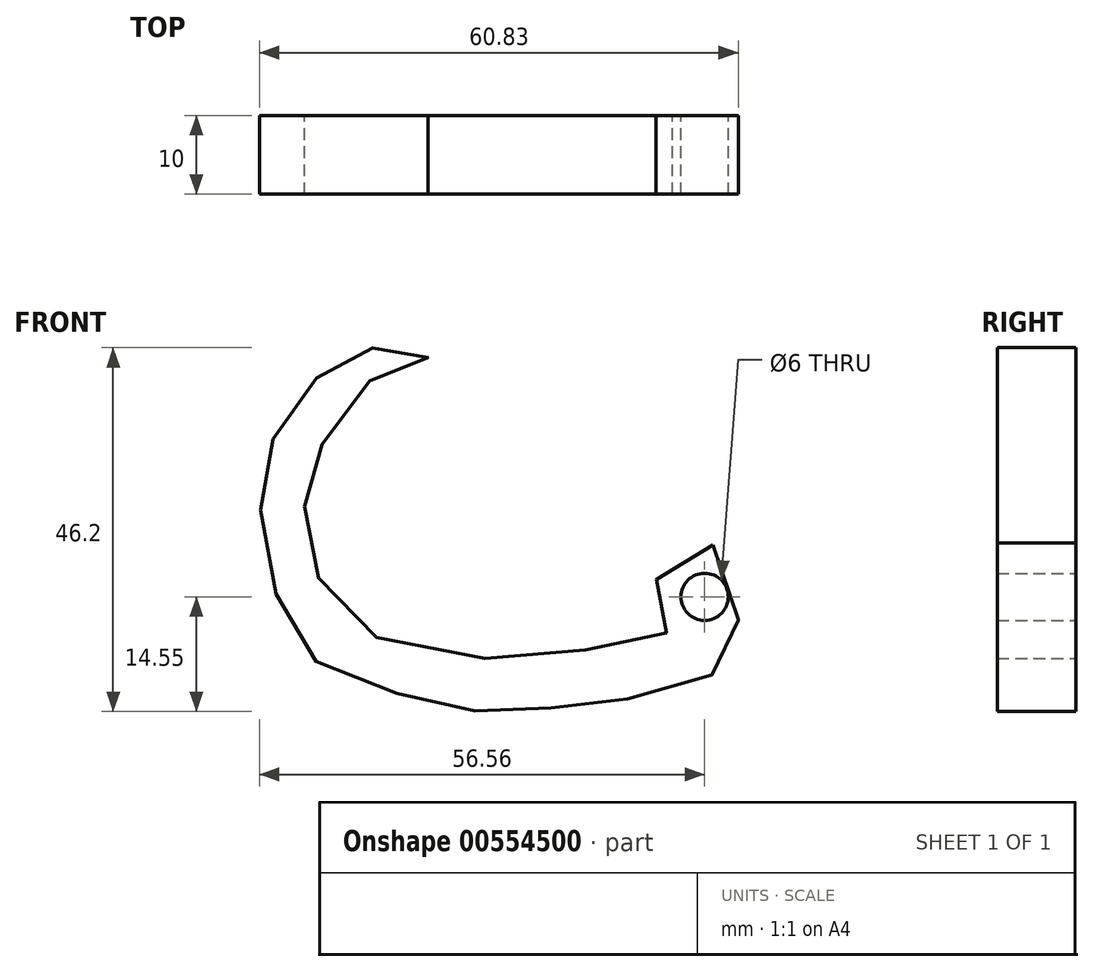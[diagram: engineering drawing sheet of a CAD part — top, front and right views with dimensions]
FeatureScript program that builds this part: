
annotation { "Feature Type Name" : "Feature", "Feature Type Description" : "" }
export const myFeature = defineFeature(function(context is Context, id is Id, definition is map)
    precondition{}
    {
        {
            var Q0;
            Q0=qCreatedBy(makeId("Front.planeOp"),FACE);
            var sketch = newSketch(context, id + "F0", { "sketchPlane" : qUnion([Q0])});
            skFitSpline(sketch, "E0", {"points": [v(32.44, 3.87) * mm, v(35.6, -6.2) * mm, v(33.3, -11.94) * mm, v(21.51, -15.68) * mm, v(11.45, -16.83) * mm, v(1.67, -17.12) * mm, v(-9.26, -14.53) * mm, v(-20.19, -9.07) * mm, v(-23.92, 1.86) * mm, v(-25.08, 12.79) * mm, v(-21.34, 20.7) * mm, v(-15.3, 27.45) * mm, v(-8.68, 28.9) * mm, v(-3.8, 27.74) * mm, v(-8.68, 26.3) * mm, v(-16.16, 18.54) * mm, v(-19.32, 11.35) * mm, v(-18.75, 3.59) * mm, v(-14.15, -5.62) * mm, v(3.97, -10.5) * mm, v(20.36, -8.78) * mm, v(27.26, -6.2) * mm, v(25.25, 0.14) * mm, v(32.44, 3.87) * mm]});
            skCircle(sketch, "E1", {"center": v(31.35, -2.7) * mm, "radius": 3 * mm});
            skSolve(sketch);
        }
        {
            var Q0;
            Q0=makeQuery(id+"F0.imprint","IMPRINT",FACE,{"disambiguationData":[TD([[makeQuery(id+"F0.imprint","IMPRINT",EDGE,{"derivedFrom":sQuery(id+"F0.wireOp",EDGE,"E0")}),-1.0]])]});
            extrude(context, id + "F1", {"entities" : qUnion([Q0]), "depth" : 10 * mm, "offsetDistance" : 25 * mm});
        }
    });
